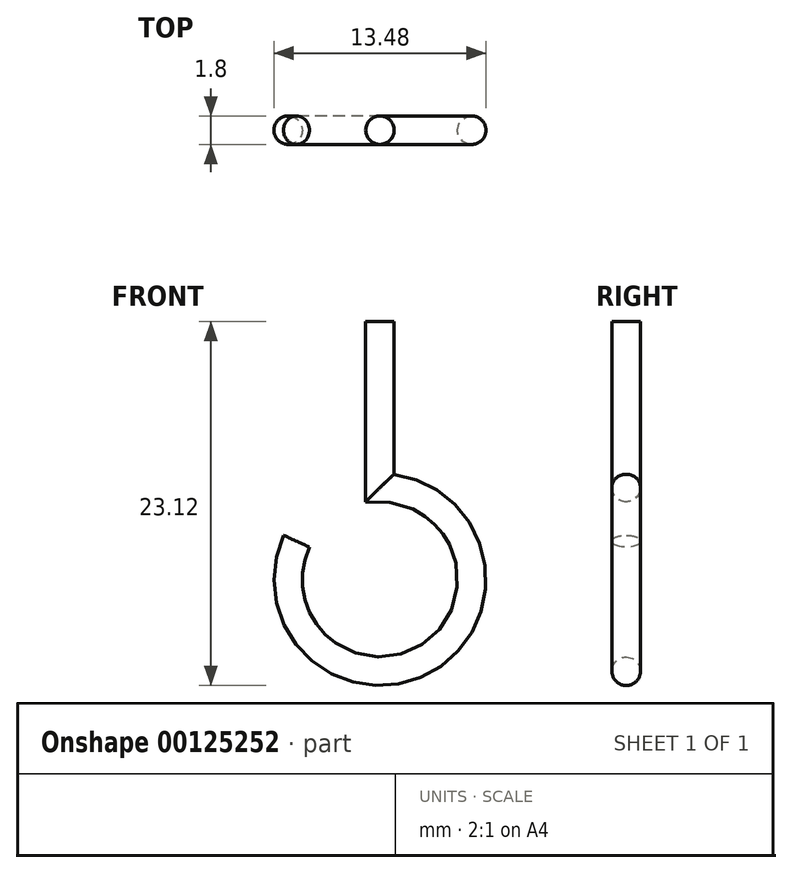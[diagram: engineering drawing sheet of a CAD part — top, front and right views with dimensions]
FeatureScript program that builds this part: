
annotation { "Feature Type Name" : "Feature", "Feature Type Description" : "" }
export const myFeature = defineFeature(function(context is Context, id is Id, definition is map)
    precondition{}
    {
        {
            var Q0;
            Q0=qCreatedBy(makeId("Front.planeOp"),FACE);
            var sketch = newSketch(context, id + "F0", { "sketchPlane" : qUnion([Q0])});
            skLineSegment(sketch, "E0", {"start": v(0, 0) * mm, "end": v(0, -10.55) * mm});
            skArc(sketch, "E1", {"start": v(-5.3, -13.95) * mm, "mid": v(3.15, -21.3) * mm, "end": v(0, -10.55) * mm});
            skLineSegment(sketch, "E2", {"start": v(0, -16.3) * mm, "end": v(0, -16.38) * mm});
            skSolve(sketch);
        }
        {
            var Q0;
            Q0=qCreatedBy(makeId("Top.planeOp"),FACE);
            var sketch = newSketch(context, id + "F1", { "sketchPlane" : qUnion([Q0])});
            skCircle(sketch, "E3", {"center": v(0, 0) * mm, "radius": 0.9 * mm});
            skSolve(sketch);
        }
        {
            var Q0;
            Q0=makeQuery(id+"F1.imprint","IMPRINT",FACE,{"disambiguationData":[TD([[makeQuery(id+"F1.imprint","IMPRINT",EDGE,{"derivedFrom":sQuery(id+"F1.wireOp",EDGE,"E3")}),1.0]])]});
            var Q1;
            Q1=sQuery(id+"F0.wireOp",EDGE,"E0");
            var Q2;
            Q2=sQuery(id+"F0.wireOp",EDGE,"E1");
            sweep(context, id + "F2", {"profiles" : qUnion([Q0]), "path" : qUnion([Q1, Q2])});
        }
    });
